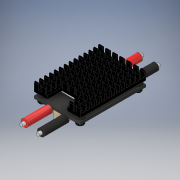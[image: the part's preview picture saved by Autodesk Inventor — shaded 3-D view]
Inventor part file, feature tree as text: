
AUTODESK INVENTOR PART (.ipt)
format: ipt  version: 2019.4 (Build 234330000, 330)  size: 1,017,856 bytes
history: native  units: mm
features: extrude x16, sketch x12, mirror x6, fillet x4, pattern_linear x2, plane x1, revolve x1, chamfer x1, projected_geometry x1
ambient origin geometry x8: Origin, YZ Plane, XZ Plane, XY Plane, X Axis, Y Axis, Z Axis, Center Point
bodies: Solid1 (feature_tree)
feature tree (44):
  extrude  "Extrusion1"  Depth=40.0mm
  extrude  "Extrusion2"  Depth=5.0mm
  extrude  "Extrusion3"  Depth=2.0mm
  extrude  "Extrusion4"  Depth=8.0mm
  extrude  "Extrusion5"  Depth=1.0mm TaperAngle=0.0deg
  fillet  "Fillet1"  Radius=0.2mm
  pattern_linear  "Rectangular Pattern1"  Count1=14 Spacing1=3.0mm
  mirror  "Mirror1"
  extrude  "Extrusion6"  Depth=2.5mm
  fillet  "Fillet2"  Radius=1.0mm
  pattern_linear  "Rectangular Pattern2"  Count1=11 Spacing1=3.0mm
  extrude  "Extrusion7"  Depth=4.5mm
  fillet  "Fillet3"  Radius=2.0mm
  extrude  "Extrusion8"  Depth=1.0mm
  mirror  "Mirror2"
  mirror  "Mirror3"
  sketch  "Sketch9"  dims[d19=0.5mm d20=140.0mm d22=3.0mm]
  extrude  "Extrusion9"  Depth=1.0mm
  fillet  "Fillet4"  Radius=4.0mm
  mirror  "Mirror4"
  plane  "Work Plane1"
  revolve  "Revolution1"  [1 undecoded]
  mirror  "Mirror5"
  mirror  "Mirror6"
  extrude  "Extrusion10"  Depth=1.5mm TaperAngle=0.0deg
  extrude  "Extrusion11"  Depth=5.0mm
  extrude  "Extrusion12"  Depth=8.0mm
  extrude  "Extrusion13"  Depth=1.0mm
  extrude  "Extrusion14"  Depth=6.0mm
  chamfer  "Chamfer1"  Distance=4.0mm
  extrude  "Extrusion15"  Depth=1.0mm
  extrude  "Extrusion16"  Depth=0.5mm
  sketch  "Sketch1"  dims[d0=28.0mm d1=40.0mm]
  sketch  "Sketch2"  dims[d2=1.57mm d3=0.0mm d4=5.0mm]
  sketch  "Sketch3"  dims[d5=2.0mm d6=0.0mm d7=9.0mm]
  sketch  "Sketch4"  dims[d8=8.0mm d9=8.0mm]
  projected_geometry  "Projected Loop1"
  sketch  "Sketch5"  dims[d10=2.0mm d11=0.0mm d12=1.0mm d13=0.0mm d14=0.2mm]
  sketch  "Sketch6"  dims[d15=1.0mm]
  sketch  "Sketch7"  dims[d16=2.5mm]
  sketch  "Sketch8"  dims[d17=3.5mm d18=0.0mm]
  sketch  "Sketch10"  dims[d23=20.0mm d25=4.25mm d26=2.5mm d27=1.0mm]
  sketch  "Sketch11"  dims[d28=3.5mm d29=0.0mm]
  sketch  "Sketch12"  dims[d30=0.5mm d31=110.0mm d33=3.0mm d34=30.0mm d36=4.25mm d37=4.5mm d38=2.0mm d39=0.0mm d40=1.0mm d41=1.0mm d42=4.0mm d43=1.0mm d44=1.5mm d45=0.0mm d46=5.0mm d47=8.0mm d48=0.1mm d49=6.0mm d50=4.0mm d51=0.1mm d52=0.5mm d53=3.0mm d54=0.0mm d55=1.999992mm d59=1.0265mm d60=2.0mm d61=20.0mm d62=90.0deg d63=2.25mm d64=0.5mm d65=1.0mm d66=1.0mm d67=0.5mm d68=0.5mm d70=0.3mm d71=0.5mm d72=0.5mm d73=0.5mm d74=0.5mm d75=1.48mm d76=1.0mm d77=0.0mm d78=6.0mm d79=0.0mm d80=4.0mm d81=0.0mm d82=1.5mm d83=0.0mm d84=5.0mm d85=0.0mm d86=0.2mm d87=2.0mm d88=45.0deg d89=0.5mm d90=0.5mm d91=1.0mm d92=6.0mm d93=0.0mm d94=1.0mm d95=2.0mm d97=0.5mm d98=2.0mm d99=6.0mm d100=0.0mm d101=1.0mm]
note: 1 required parameter value undecoded (feature->parameter linkage not recoverable at this tier; creation-order binding heuristic only, values carry confidence <= 0.55)
